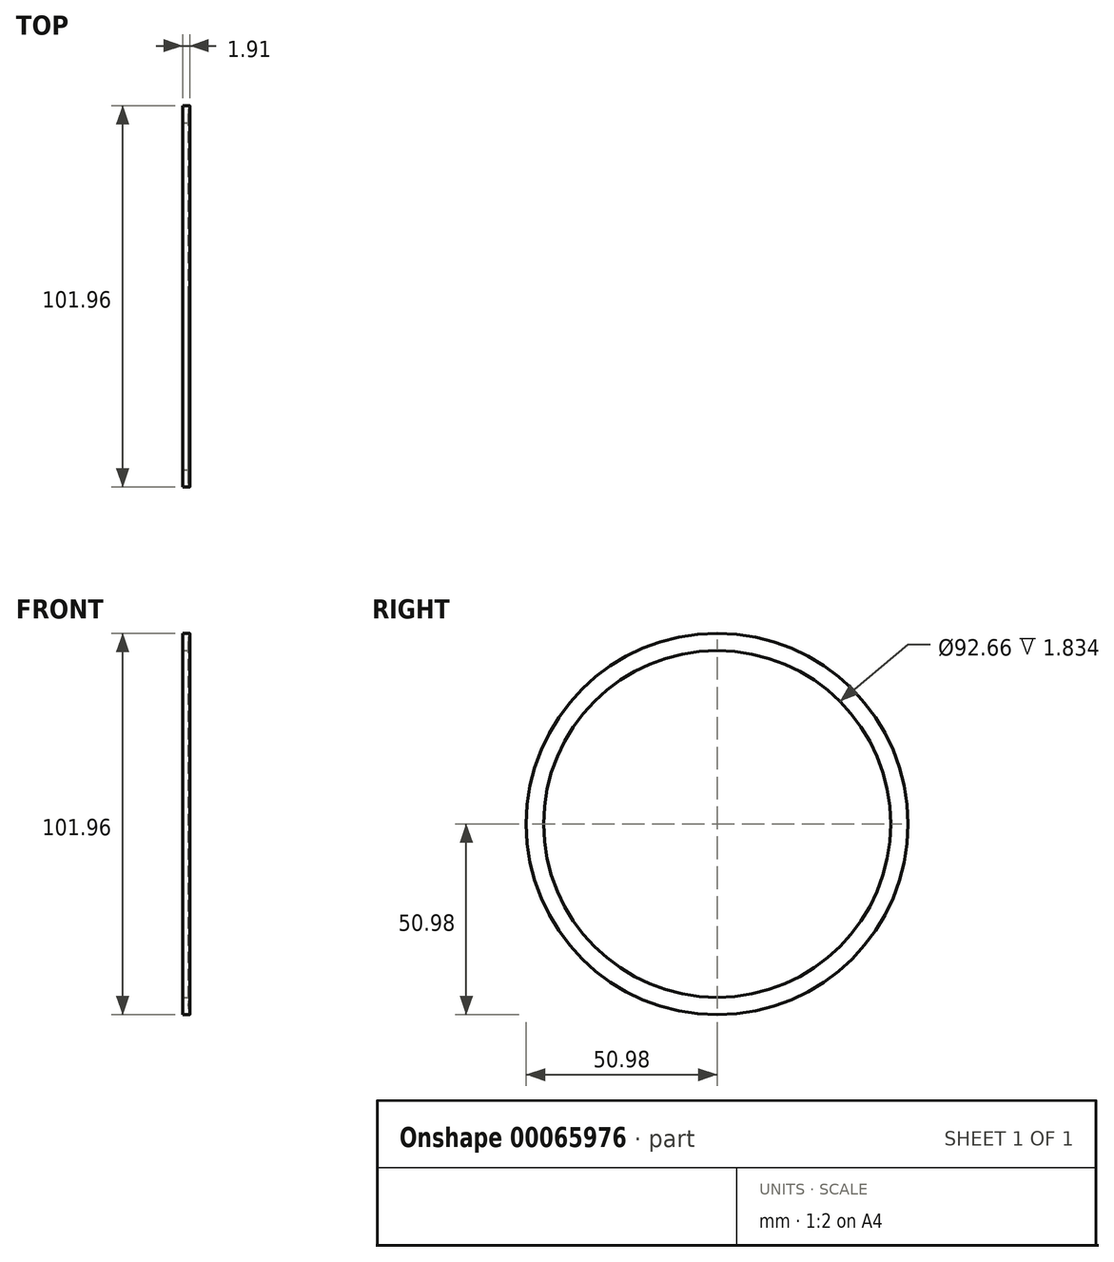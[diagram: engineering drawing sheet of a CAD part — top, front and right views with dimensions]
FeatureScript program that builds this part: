
annotation { "Feature Type Name" : "Feature", "Feature Type Description" : "" }
export const myFeature = defineFeature(function(context is Context, id is Id, definition is map)
    precondition{}
    {
        {
            var Q0;
            Q0=qCreatedBy(makeId("Front.planeOp"),FACE);
            var sketch = newSketch(context, id + "F0", { "sketchPlane" : qUnion([Q0])});
            skLineSegment(sketch, "E0.bottom", {"start": v(-0.1, 50.98) * mm, "end": v(-1.94, 50.98) * mm});
            skLineSegment(sketch, "E0.top", {"start": v(-0.1, 46.33) * mm, "end": v(-1.94, 46.33) * mm});
            skLineSegment(sketch, "E0.right", {"start": v(-1.94, 50.98) * mm, "end": v(-1.94, 46.33) * mm});
            skLineSegment(sketch, "E1", {"start": v(0, 0) * mm, "end": v(-6.16, 0) * mm, "construction": true});
            skArc(sketch, "E2", {"start": v(-0.04, 50.88) * mm, "mid": v(-0.42, 48.65) * mm, "end": v(-0.04, 46.43) * mm});
            skPoint(sketch, "E3.visualSharp", {"position": v(0, 50.98) * mm});
            skArc(sketch, "E3.filletArc", {"start": v(-0.04, 50.88) * mm, "mid": v(-0.05, 50.95) * mm, "end": v(-0.1, 50.98) * mm});
            skPoint(sketch, "E4.visualSharp", {"position": v(0, 46.33) * mm});
            skArc(sketch, "E4.filletArc", {"start": v(-0.1, 46.33) * mm, "mid": v(-0.05, 46.36) * mm, "end": v(-0.04, 46.43) * mm});
            skLineSegment(sketch, "E5", {"start": v(0, 46.33) * mm, "end": v(0, 0) * mm, "construction": true});
            skSolve(sketch);
        }
        {
            var Q0;
            Q0=makeQuery(id+"F0.imprint","IMPRINT",FACE,{"disambiguationData":[TD([[makeQuery(id+"F0.imprint","IMPRINT",EDGE,{"derivedFrom":sQuery(id+"F0.wireOp",EDGE,"E0.bottom")}),1.0]])]});
            var Q1;
            Q1=sQuery(id+"F0.wireOp",EDGE,"E1");
            revolve(context, id + "F1", {"entities" : qUnion([Q0]), "axis" : qUnion([Q1]), "revolveType" : RevolveType.FULL});
        }
    });
